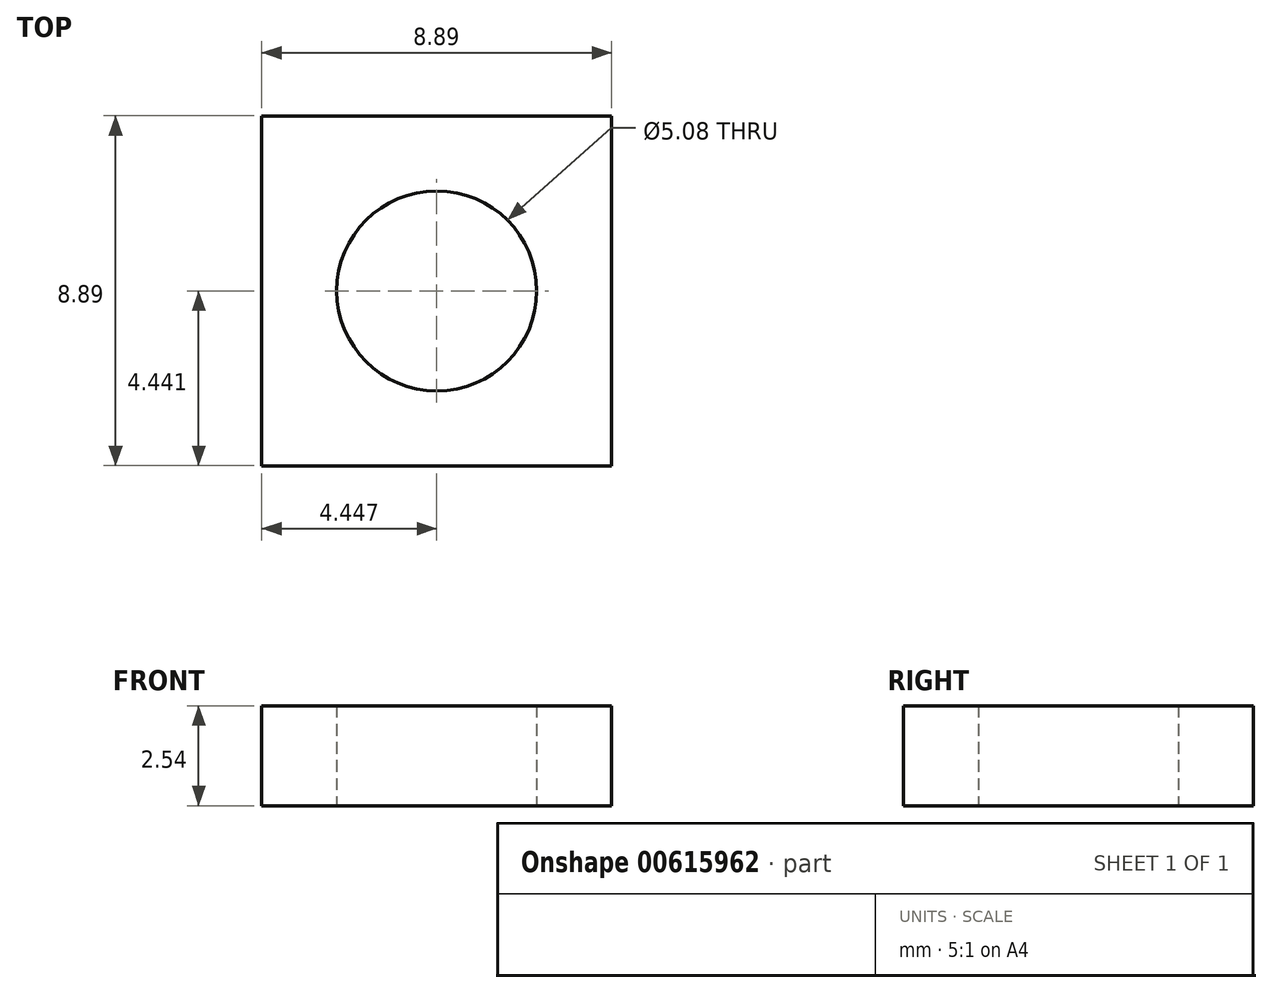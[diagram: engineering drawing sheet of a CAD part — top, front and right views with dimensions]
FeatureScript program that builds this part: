
annotation { "Feature Type Name" : "Feature", "Feature Type Description" : "" }
export const myFeature = defineFeature(function(context is Context, id is Id, definition is map)
    precondition{}
    {
        {
            var Q0;
            Q0=qCreatedBy(makeId("Top.planeOp"),FACE);
            var sketch = newSketch(context, id + "F0", { "sketchPlane" : qUnion([Q0])});
            skLineSegment(sketch, "E0.bottom", {"start": v(-25.57, 19.47) * mm, "end": v(-16.68, 19.47) * mm});
            skLineSegment(sketch, "E0.top", {"start": v(-25.57, 10.58) * mm, "end": v(-16.68, 10.58) * mm});
            skLineSegment(sketch, "E0.left", {"start": v(-25.57, 19.47) * mm, "end": v(-25.57, 10.58) * mm});
            skLineSegment(sketch, "E0.right", {"start": v(-16.68, 19.47) * mm, "end": v(-16.68, 10.58) * mm});
            skCircle(sketch, "E1", {"center": v(-21.12, 15.02) * mm, "radius": 2.54 * mm});
            skSolve(sketch);
        }
        {
            var Q0;
            Q0 = qSketchRegion(id + "F0", true);
            extrude(context, id + "F1", {"entities" : qUnion([Q0]), "depth" : 2.54 * mm, "offsetDistance" : 25.4 * mm});
        }
    });
